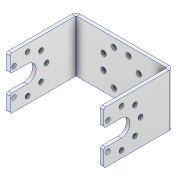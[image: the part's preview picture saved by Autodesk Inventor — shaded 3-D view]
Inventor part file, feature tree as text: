
AUTODESK INVENTOR PART (.ipt)
format: ipt  version: 2020 (Build 240168000, 168)  size: 214,016 bytes
history: native  units: mm
features: other x8, sketch x5, extrude x2
ambient origin geometry x8: Origin, YZ Plane, XZ Plane, XY Plane, X Axis, Y Axis, Z Axis, Center Point
bodies: Body1 (feature_tree)
feature tree (15):
  other  "솔리드1"
  other  "플랜지1"
  other  "플랜지2"
  extrude  "돌출1"  Depth=56.0mm
  extrude  "돌출2"  Depth=30.0mm
  other  "모서리 라운드1"
  sketch  "스케치1"
  sketch  "스케치2"
  other  "절곡부1"
  other  "구석1"
  sketch  "스케치3"
  other  "절곡부2"
  other  "구석2"
  sketch  "스케치4"
  sketch  "스케치5"
